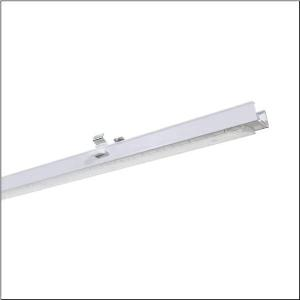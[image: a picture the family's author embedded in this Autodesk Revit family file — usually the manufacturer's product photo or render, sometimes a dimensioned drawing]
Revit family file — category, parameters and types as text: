
# Revit family: trunking_flex_31_51re12mb58b
name_source: partatom
category: Lighting Fixtures
units: mm (PartAtom-declared; Revit-internal decimal feet)

## family parameters
Cut with Voids When Loaded = No
Host = Face
Light Source = No
Part Type = Normal
Room Calculation Point = No
Round Connector Dimension = Use Diameter
Shared = No

## types (1)
- --- (1 x LED, 8000 lm, 50 W, 5000K)
    Apparent Load = 50 VA
    CIE Flux Codes = 65 91 98 99 100
    Color Rendering = 80
    Color Temperature = 5000K
    Default Elevation = 1800 mm
    Description = Trunking Flex 31, luminaire insert, of extruded aluminium section, coated, traffic white (RAL 9016), length: 1.472mm, width: 91mm, height: 53mm, LED rated luminous flux: 8.000lm, light colour: 850, control gear: ON/OFF Multilumen, with system connector: socket, mains connection: 220..240V, AC, 50/60Hz, rated input power: 50W, luminous flux adjustable on luminaire in four steps (4130/5610/6850/8000lm), connected load according to luminous flux setting (25/34/42/50W), primary light control with lens, of plastic, primary optical cover: cover, of PMMA, light emission: direct distribution, protection rating (complete): IP20, insulation class (complete): insulation class I (protective earthing), certification: CE, UKCA, impact resistance: IK02, permissible ambient temperature for indoor applications: -20..+40°C, packaging unit: 1 piece
    Height = 58 mm
    Lamp = 1 x LED
    Lamp Light Flux = 8000 lm
    Lamp Power = 50 W
    Lamp count = 1
    Length = 1472 mm
    Luminous efficacy = 160 lm/W
    Manufacturer = Siteco
    ModVariant = No
    Model = 51RE12MB58B
    Mounting Place = Ceiling
    Mounting Type = Pendant
    Number of Poles = 1
    OnlyDefault = Yes
    Power Factor = 1
    Product Name = Trunking Flex 31
    Product group = luminaire insert
    ProductGroupID = 901
    Protection Class = Protection class I
    Protection Degree = IP 20
    RLX_Detail_Level = 1
    RLX_Emergency_Light_Flux = 0 lm
    RLX_Emergency_Type = 0
    RLX_Emergency_Type_DB = No
    RlxData = <blob elided: 20349 chars, md5=4cfc1ce0>
    Socket = socket
    Standby Power = 0 W
    System Light Flux = 8000 lm
    System Power = 50 W
    Type Comments = factory setting: luminous flux: 100 % | (ON | ON) | 300 mA
    Type Image = l_1266702.jpg
    URL = http://relux.com
    VarID = @adj_001249
    Voltage = 0 V
    Weight = 0.00 kg
    Width = 65 mm

## geometry (parser evidence)
native form markers: Blend x4, Sweep x13
no freeform markers — native parametric forms only
